# Revit family: UNB_Eurovit+_R0271_BIM_NL
name_source: partatom
category: Plumbing Fixtures
units: mm (PartAtom-declared; Revit-internal decimal feet)

## family parameters
Cut with Voids When Loaded = No
Host = Face
Maintain Annotation Orientation = No
OmniClass Number = 23.45.05.14.21.11
OmniClass Title = Bath/Shower Units
Part Type = Normal
Room Calculation Point = No
Round Connector Dimension = Use Diameter
Shared = Yes

## types (4) — shared parameters
Accesoires = https://www.idealstandard.nl
Accessories = https://www.idealstandard.nl
Afmetingen = 355 x 202 x 550 mm
AfstandsEenheid = millimeter
AreaUnits = millimeter
Assembly Code = C1030200
AssetType = Vast
Auteur = Ideal Standard
BIMObjectName = ISI_IdealStandard_Furniture_R0271
BREEAM = No
BimObjectNaam = ISI_IdealStandard_Furniture_R0271
Brand = Unbranded
Breedte = 354
ConnectionType = sanitair
CurrencyUnit = €
Default Elevation = 1219 mm
Diepte = 201,999999999992
DurationUnit = jaar
DuurEenheid = jaar
ECA = No
EPD = https://www.idealstandard.nl
ExpectedLife = 30
GemaaktOp = 26/06/2024
Help = https://www.idealstandard.nl
Hoogte = 550,000000000002
Hulp = https://www.idealstandard.nl
IfcExportAs = IfcFurnitureType
Installatieinstructies = https://www.idealstandard.nl
InstallationInstructions = https://www.idealstandard.nl
Lengte = 201,999999999992
LinearUnits = millimeters
Manufacturer = Ideal Standard
ManufacturerURL = https://www.idealstandard.nl
Materiaal = Furniture
Merk = Merkloos
NBSDescription = Baths
Name = ISI_Furniture_Unb_R0271_IdealStandard
NettWeight = Kg
Nettogewicht = Kg
NominalDepth = 202 mm  [stored 0.66273 ft]
NominalHeight = 550 mm
NominalLength = 202 mm  [stored 0.66273 ft]
NominalWidth = 354 mm
ProductInformation = https://www.idealstandard.nl
ProductSoort = meubels
Productinformatie = https://www.idealstandard.nl
Shape = Rechthoekig
Size = 355 x 202 x 550 mm
Space = Intern
SpareParts = https://www.idealstandard.nl
TMV3 = No
Telefoonnummer = 077 355 08 08
Typeconnectie = sanitair
URL = https://www.idealstandard.nl
Uniclass2015Code = Pr_40_20_76
Uniclass2015Title = Sanitary accessories
Uniclass2015Version = Products v1.34
Urlproducent = https://www.idealstandard.nl
ValutaEenheid = €
Versie = 1
Version = 1
VolumeUnits = Liter
Volumeunits = Liter
Vorm = Rechthoekig
WRAS = No
WaarborgGarantieInstallatie = Fabrieksgarantie
WarrantyDescription = Manufacturers Warranty
WarrantyDurationParts = 2
WarrantyDurationUnit = year
WarrantyGuarantorParts = https://www.idealstandard.nl
WaterEfficientProduct = No
Wisselstukken = https://www.idealstandard.nl
zero-valued in all types: Vervangingskosten

## per-type parameters (varying)
| type | Afwerking | Artikelnummer | Artikelomschrijving | BarCode | Color | Description | Eigenschappen | Features | Finish | Kleur | MAT | Model | ModelNumber | ModelReference |
| R0271WG - GUEST UNIT 36x21 1 DOOR GLOSSY WHITE | Glanzend wit | R0271WG | Eurovit 2.0 GASTENTOESTEL 36x21 WANDHANGING 1 DEUR GLANZEND WIT | 3391500589278 | Glanzend wit | Eurovit 2.0 GASTENTOESTEL 36x21 WANDHANGING 1 DEUR GLANZEND WIT | Eurovit 2.0 GASTENTOESTEL 36x21 WANDHANGING 1 DEUR GLANZEND WIT | Eurovit 2.0 GASTENTOESTEL 36x21 WANDHANGING 1 DEUR GLANZEND WIT | Glanzend wit | Glanzend wit | WG-White | R0271WG | R0271WG | Eurovit 2.0 GASTENTOESTEL 36x21 WANDHANGING 1 DEUR GLANZEND WIT |
| R0271TI - GUEST UNIT 36x21 1 DOOR MID GREY | Middengrijs | R0271TI | Eurovit 2.0 GASTENTOESTEL 36x21 WANDHANGEND 1 DEUR MIDDENGRIJS | 3391500589261 | Middengrijs | Eurovit 2.0 GASTENTOESTEL 36x21 WANDHANGEND 1 DEUR MIDDENGRIJS | Eurovit 2.0 GASTENTOESTEL 36x21 WANDHANGEND 1 DEUR MIDDENGRIJS | Eurovit 2.0 GASTENTOESTEL 36x21 WANDHANGEND 1 DEUR MIDDENGRIJS | Middengrijs | Middengrijs | TI | R0271TI | R0271TI | Eurovit 2.0 GASTENTOESTEL 36x21 WANDHANGEND 1 DEUR MIDDENGRIJS |
| R0271Y8 - GUEST UNIT 36x21 1 DOOR NATURAL OAK | Natuurlijk eiken | R0271Y8 | Eurovit 2.0 GASTENTOESTEL 36x21 WANDHANGEND 1 DEUR NATUURLIJK EIKEN | 3391500589285 | Natuurlijk eiken | Eurovit 2.0 GASTENTOESTEL 36x21 WANDHANGEND 1 DEUR NATUURLIJK EIKEN | Eurovit 2.0 GASTENTOESTEL 36x21 WANDHANGEND 1 DEUR NATUURLIJK EIKEN | Eurovit 2.0 GASTENTOESTEL 36x21 WANDHANGEND 1 DEUR NATUURLIJK EIKEN | Natuurlijk eiken | Natuurlijk eiken | Y8 | R0271Y8 | R0271Y8 | Eurovit 2.0 GASTENTOESTEL 36x21 WANDHANGEND 1 DEUR NATUURLIJK EIKEN |
| R0271Y9 - GUEST UNIT 36x21 1 DOOR FLINT HICKORY | Flint-Hickory | R0271Y9 | Eurovit 2.0 GASTENTOESTEL 36x21 WANDHANGEND 1 DEUR FLINT HICKORY | 3391500589292 | Flint-Hickory | Eurovit 2.0 GASTENTOESTEL 36x21 WANDHANGEND 1 DEUR FLINT HICKORY | Eurovit 2.0 GASTENTOESTEL 36x21 WANDHANGEND 1 DEUR FLINT HICKORY | Eurovit 2.0 GASTENTOESTEL 36x21 WANDHANGEND 1 DEUR FLINT HICKORY | Flint-Hickory | Flint-Hickory | Y9 | R0271Y9 | R0271Y9 | Eurovit 2.0 GASTENTOESTEL 36x21 WANDHANGEND 1 DEUR FLINT HICKORY |

note: [stored X ft] marks values corroborated as IEEE doubles in the binary element streams (Revit-internal decimal feet)

## geometry (parser evidence)
native form markers: Sweep x2
no freeform markers — native parametric forms only
